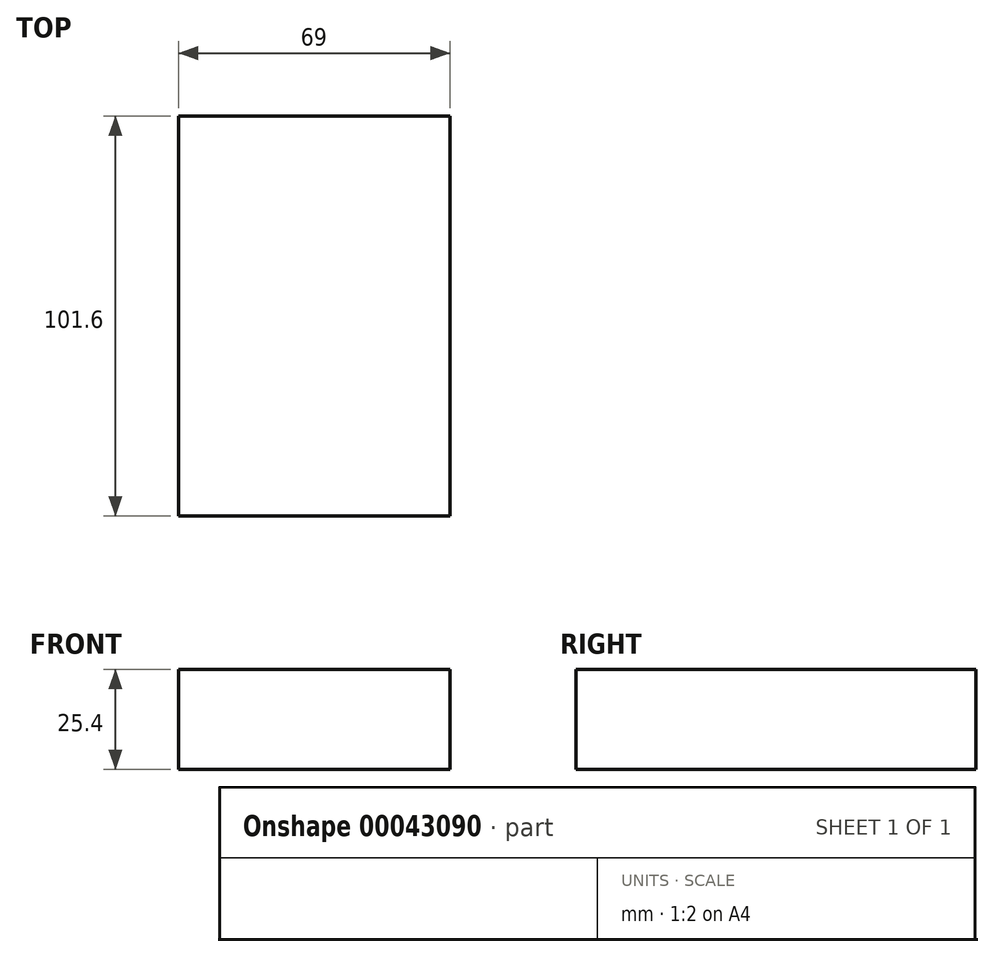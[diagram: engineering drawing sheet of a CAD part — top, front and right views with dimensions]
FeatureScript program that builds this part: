
annotation { "Feature Type Name" : "Feature", "Feature Type Description" : "" }
export const myFeature = defineFeature(function(context is Context, id is Id, definition is map)
    precondition{}
    {
        {
            var Q0;
            Q0=qCreatedBy(makeId("Top.planeOp"),FACE);
            var sketch = newSketch(context, id + "F0", { "sketchPlane" : qUnion([Q0])});
            skLineSegment(sketch, "E0.bottom", {"start": v(-30.14, 45.52) * mm, "end": v(38.86, 45.52) * mm});
            skLineSegment(sketch, "E0.top", {"start": v(-30.14, -56.08) * mm, "end": v(38.86, -56.08) * mm});
            skLineSegment(sketch, "E0.left", {"start": v(-30.14, 45.52) * mm, "end": v(-30.14, -56.08) * mm});
            skLineSegment(sketch, "E0.right", {"start": v(38.86, 45.52) * mm, "end": v(38.86, -56.08) * mm});
            skSolve(sketch);
        }
        {
            var Q0;
            Q0 = qSketchRegion(id + "F0", true);
            extrude(context, id + "F1", {"entities" : qUnion([Q0]), "depth" : 25.4 * mm});
        }
    });
